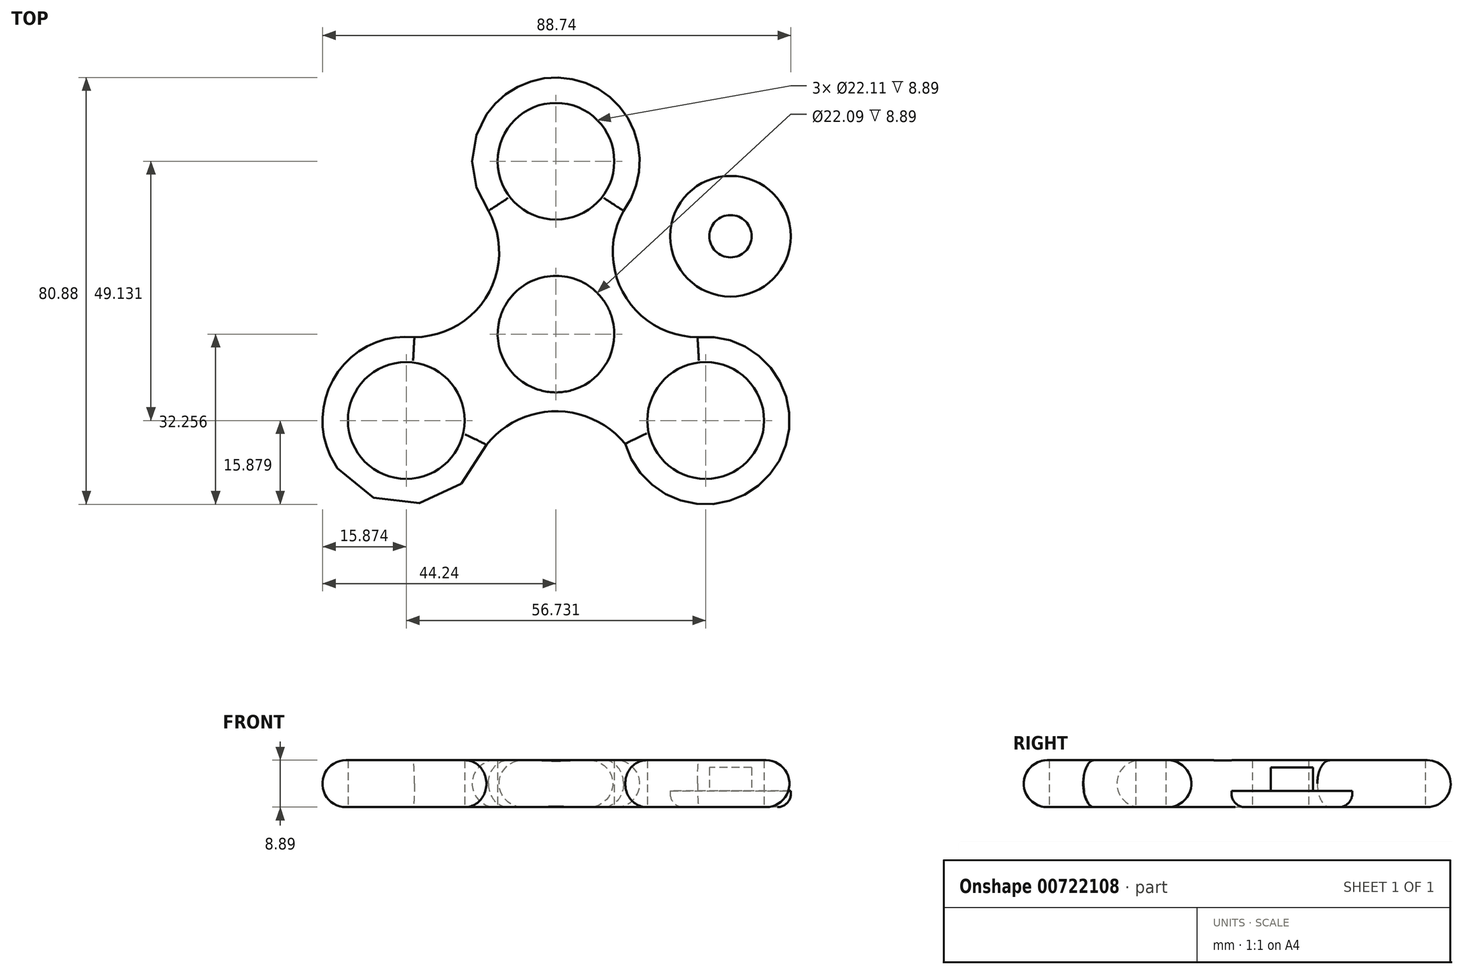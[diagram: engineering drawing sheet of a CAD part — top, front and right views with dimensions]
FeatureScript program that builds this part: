
annotation { "Feature Type Name" : "Feature", "Feature Type Description" : "" }
export const myFeature = defineFeature(function(context is Context, id is Id, definition is map)
    precondition{}
    {
        {
            var Q0;
            Q0=qCreatedBy(makeId("Top.planeOp"),FACE);
            var sketch = newSketch(context, id + "F0", { "sketchPlane" : qUnion([Q0])});
            skCircle(sketch, "E0", {"center": v(0, 61.7) * mm, "radius": 11.06 * mm});
            skCircle(sketch, "E1.1.0", {"center": v(-28.37, 12.58) * mm, "radius": 11.06 * mm});
            skCircle(sketch, "E1.2.0", {"center": v(28.37, 12.58) * mm, "radius": 11.06 * mm});
            skPoint(sketch, "E1.center", {"position": v(0, 28.96) * mm});
            skCircle(sketch, "E2", {"center": v(0, 28.96) * mm, "radius": 11.04 * mm});
            skArc(sketch, "E3", {"start": v(12.8, 52.32) * mm, "mid": v(0, 77.58) * mm, "end": v(-12.8, 52.32) * mm});
            skArc(sketch, "E4", {"start": v(-26.83, 28.38) * mm, "mid": v(-41.56, 3.75) * mm, "end": v(-13.17, 7.97) * mm});
            skArc(sketch, "E5", {"start": v(13.12, 8.14) * mm, "mid": v(41.51, 3.68) * mm, "end": v(26.83, 28.38) * mm});
            skArc(sketch, "E6", {"start": v(-26.83, 28.38) * mm, "mid": v(-12.5, 37.21) * mm, "end": v(-13.87, 54) * mm});
            skArc(sketch, "E7.MirrorCS", {"start": v(26.83, 28.38) * mm, "mid": v(12.5, 37.21) * mm, "end": v(13.87, 54) * mm});
            skArc(sketch, "E8", {"start": v(16.22, 2.35) * mm, "mid": v(0.13, 14.33) * mm, "end": v(-16.08, 2.52) * mm});
            skSolve(sketch);
        }
        {
            var Q0;
            Q0=qSketchRegion(id+"F0",true);
            extrude(context, id + "F1", {"entities" : qUnion([Q0]), "depth" : 8.9 * mm, "offsetDistance" : 25.4 * mm});
        }
        {
            var Q0;
            Q0=makeQuery(id+"F1.opExtrude","CAP_EDGE",EDGE,{"disambiguationData":[OSD([sQuery(id+"F0.wireOp",EDGE,"E8")])],"isStart":false});
            var Q1;
            Q1=makeQuery(id+"F1.opExtrude","CAP_EDGE",EDGE,{"disambiguationData":[OSD([sQuery(id+"F0.wireOp",EDGE,"E4")])],"isStart":false});
            var Q2;
            Q2=makeQuery(id+"F1.opExtrude","CAP_EDGE",EDGE,{"disambiguationData":[OSD([sQuery(id+"F0.wireOp",EDGE,"E6")])],"isStart":false});
            var Q3;
            Q3=makeQuery(id+"F1.opExtrude","CAP_EDGE",EDGE,{"disambiguationData":[OSD([sQuery(id+"F0.wireOp",EDGE,"E3")])],"isStart":false});
            var Q4;
            Q4=makeQuery(id+"F1.opExtrude","CAP_EDGE",EDGE,{"disambiguationData":[OSD([sQuery(id+"F0.wireOp",EDGE,"E5")])],"isStart":false});
            var Q5;
            Q5=makeQuery(id+"F1.opExtrude","CAP_EDGE",EDGE,{"disambiguationData":[OSD([sQuery(id+"F0.wireOp",EDGE,"E7.MirrorCS")])],"isStart":false});
            var Q6;
            Q6=makeQuery(id+"F1.opExtrude","CAP_EDGE",EDGE,{"disambiguationData":[OSD([sQuery(id+"F0.wireOp",EDGE,"E7.MirrorCS")])],"isStart":true});
            var Q7;
            Q7=makeQuery(id+"F1.opExtrude","CAP_EDGE",EDGE,{"disambiguationData":[OSD([sQuery(id+"F0.wireOp",EDGE,"E3")])],"isStart":true});
            var Q8;
            Q8=makeQuery(id+"F1.opExtrude","CAP_EDGE",EDGE,{"disambiguationData":[OSD([sQuery(id+"F0.wireOp",EDGE,"E5")])],"isStart":true});
            var Q9;
            Q9=makeQuery(id+"F1.opExtrude","CAP_EDGE",EDGE,{"disambiguationData":[OSD([sQuery(id+"F0.wireOp",EDGE,"E8")])],"isStart":true});
            var Q10;
            Q10=makeQuery(id+"F1.opExtrude","CAP_EDGE",EDGE,{"disambiguationData":[OSD([sQuery(id+"F0.wireOp",EDGE,"E4")])],"isStart":true});
            var Q11;
            Q11=makeQuery(id+"F1.opExtrude","CAP_EDGE",EDGE,{"disambiguationData":[OSD([sQuery(id+"F0.wireOp",EDGE,"E6")])],"isStart":true});
            fillet(context, id + "F2", {"entities" : qUnion([Q0, Q1, Q2, Q3, Q4, Q5, Q6, Q7, Q8, Q9, Q10, Q11]), "radius" : 4.45 * mm, "tangentPropagation" : true, "allowEdgeOverflow" : false});
        }
        {
            var Q0;
            Q0=qCreatedBy(makeId("Top.planeOp"),FACE);
            var sketch = newSketch(context, id + "F3", { "sketchPlane" : qUnion([Q0])});
            skCircle(sketch, "E9", {"center": v(33.07, 47.5) * mm, "radius": 11.43 * mm});
            skSolve(sketch);
        }
        {
            var Q0;
            Q0=makeQuery(id+"F3.imprint","IMPRINT",FACE,{"disambiguationData":[TD([[makeQuery(id+"F3.imprint","IMPRINT",EDGE,{"derivedFrom":sQuery(id+"F3.wireOp",EDGE,"E9")}),1.0]])]});
            extrude(context, id + "F4", {"entities" : qUnion([Q0]), "depth" : 3.05 * mm, "offsetDistance" : 25.4 * mm});
        }
        {
            var Q0;
            Q0=makeQuery(id+"F4.opExtrude","CAP_FACE",FACE,{"disambiguationData":[OSD([sQuery(id+"F3.wireOp",EDGE,"E9")])],"isStart":false});
            var sketch = newSketch(context, id + "F5", { "sketchPlane" : qUnion([Q0])});
            skCircle(sketch, "E10", {"center": v(33.07, 47.5) * mm, "radius": 4 * mm});
            skSolve(sketch);
        }
        {
            var Q0;
            Q0=makeQuery(id+"F5.imprint","IMPRINT",FACE,{"disambiguationData":[TD([[makeQuery(id+"F5.imprint","IMPRINT",EDGE,{"derivedFrom":sQuery(id+"F5.wireOp",EDGE,"E10")}),1.0]])]});
            extrude(context, id + "F6", {"entities" : qUnion([Q0]), "operationType" : NewBodyOperationType.ADD, "depth" : 4.44 * mm, "offsetDistance" : 25.4 * mm});
        }
        {
            var Q0;
            Q0=makeQuery(id+"F4.opExtrude","CAP_EDGE",EDGE,{"disambiguationData":[OSD([sQuery(id+"F3.wireOp",EDGE,"E9")])],"isStart":true});
            fillet(context, id + "F7", {"entities" : qUnion([Q0]), "radius" : 2.54 * mm, "tangentPropagation" : true, "allowEdgeOverflow" : false});
        }
    });
